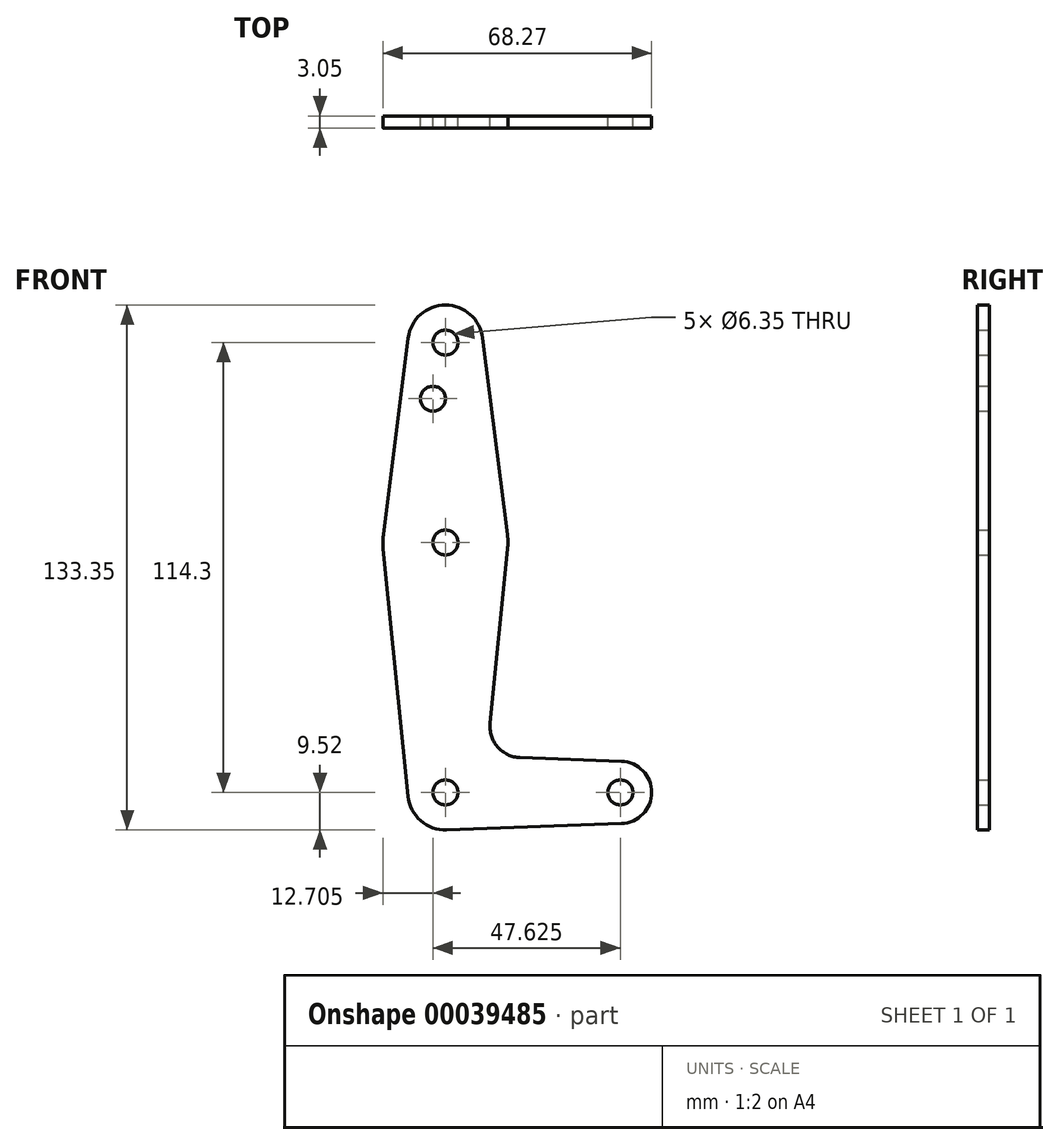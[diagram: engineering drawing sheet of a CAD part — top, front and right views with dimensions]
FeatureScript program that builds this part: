
annotation { "Feature Type Name" : "Feature", "Feature Type Description" : "" }
export const myFeature = defineFeature(function(context is Context, id is Id, definition is map)
    precondition{}
    {
        {
            var Q0;
            Q0=qCreatedBy(makeId("Front.planeOp"),FACE);
            var sketch = newSketch(context, id + "F0", { "sketchPlane" : qUnion([Q0])});
            skLineSegment(sketch, "E0", {"start": v(0, 0) * mm, "end": v(0, 114.3) * mm, "construction": true});
            skLineSegment(sketch, "E1", {"start": v(0, 0) * mm, "end": v(44.45, 0) * mm, "construction": true});
            skCircle(sketch, "E2", {"center": v(0, 114.3) * mm, "radius": 9.53 * mm});
            skCircle(sketch, "E3", {"center": v(0, 63.5) * mm, "radius": 15.88 * mm});
            skCircle(sketch, "E4", {"center": v(0, 0) * mm, "radius": 9.53 * mm});
            skCircle(sketch, "E5", {"center": v(44.45, 0) * mm, "radius": 7.94 * mm});
            skLineSegment(sketch, "E6", {"start": v(-9.45, 115.5) * mm, "end": v(-15.75, 65.48) * mm});
            skLineSegment(sketch, "E7", {"start": v(-15.8, 61.91) * mm, "end": v(-9.48, -0.95) * mm});
            skLineSegment(sketch, "E8", {"start": v(15.8, 61.91) * mm, "end": v(11.34, 17.6) * mm});
            skLineSegment(sketch, "E9", {"start": v(9.45, 115.5) * mm, "end": v(15.75, 65.48) * mm});
            skLineSegment(sketch, "E10", {"start": v(0.34, -9.52) * mm, "end": v(44.73, -7.93) * mm});
            skLineSegment(sketch, "E11", {"start": v(44.73, 7.93) * mm, "end": v(18.97, 8.85) * mm});
            skCircle(sketch, "E12", {"center": v(0, 114.3) * mm, "radius": 3.18 * mm});
            skCircle(sketch, "E13", {"center": v(0, 63.5) * mm, "radius": 3.18 * mm});
            skCircle(sketch, "E14", {"center": v(0, 0) * mm, "radius": 3.18 * mm});
            skCircle(sketch, "E15", {"center": v(44.45, 0) * mm, "radius": 3.18 * mm});
            skCircle(sketch, "E16", {"center": v(-3.18, 100.03) * mm, "radius": 3.18 * mm});
            skArc(sketch, "E17.filletArc", {"start": v(11.34, 17.6) * mm, "mid": v(13.26, 11.57) * mm, "end": v(18.97, 8.85) * mm});
            skSolve(sketch);
        }
        {
            var Q0;
            Q0 = qSketchRegion(id + "F0", true);
            extrude(context, id + "F1", {"entities" : qUnion([Q0]), "depth" : 3.05 * mm});
        }
    });
